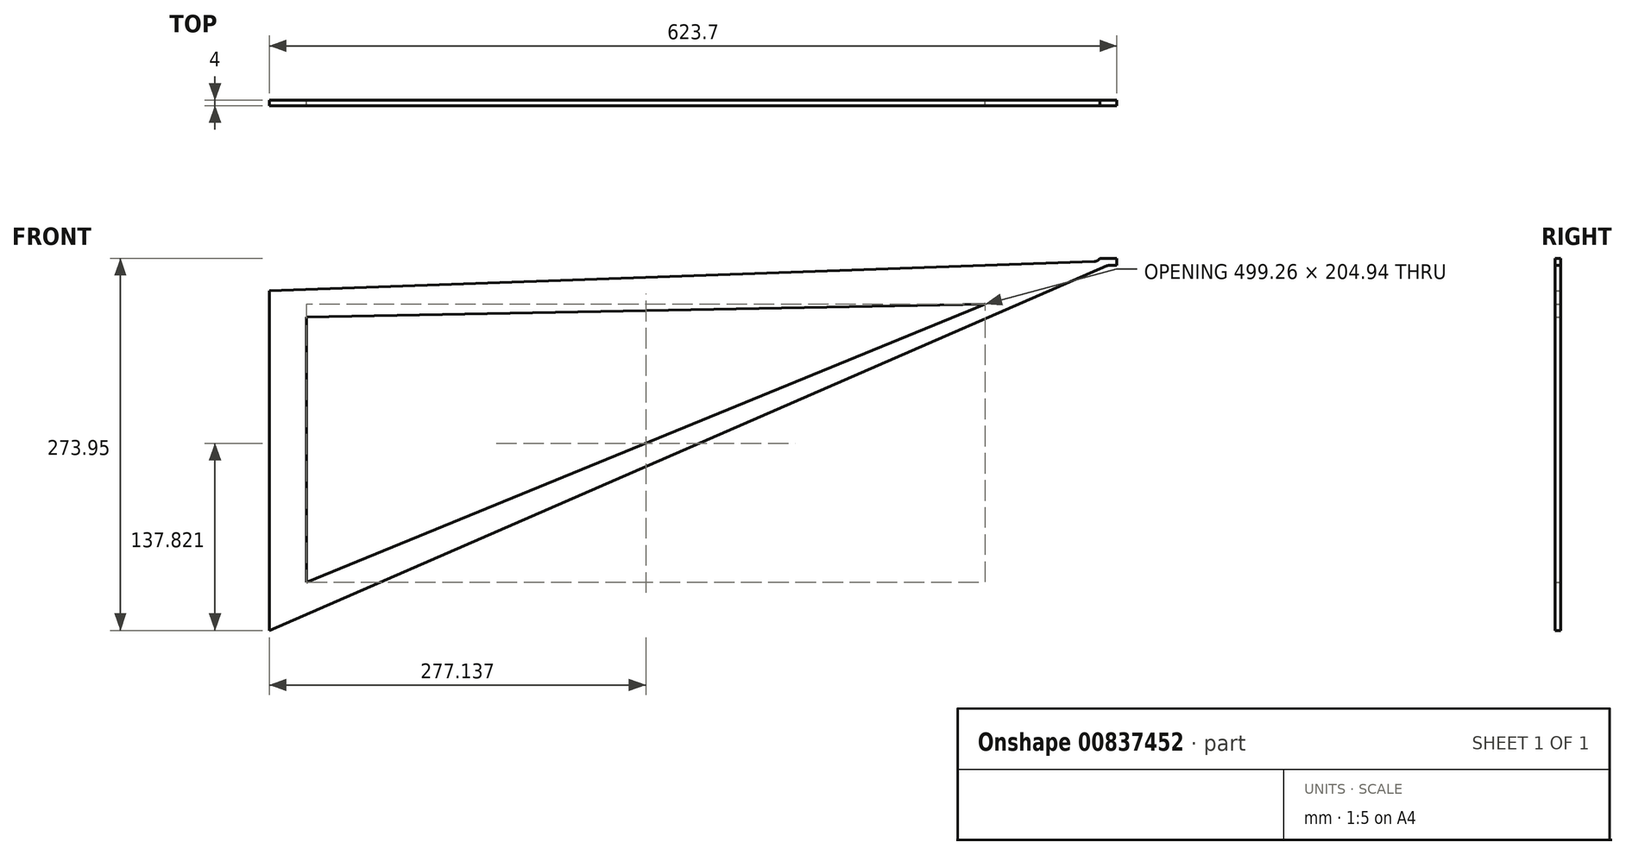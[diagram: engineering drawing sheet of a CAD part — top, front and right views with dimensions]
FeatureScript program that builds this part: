
annotation { "Feature Type Name" : "Feature", "Feature Type Description" : "" }
export const myFeature = defineFeature(function(context is Context, id is Id, definition is map)
    precondition{}
    {
        {
            var Q0;
            Q0=qCreatedBy(makeId("Front.planeOp"),FACE);
            var sketch = newSketch(context, id + "F0", { "sketchPlane" : qUnion([Q0])});
            skLineSegment(sketch, "E0", {"start": v(0, 0) * mm, "end": v(0, -250) * mm});
            skLineSegment(sketch, "E1", {"start": v(611.2, 21.85) * mm, "end": v(0, 0) * mm});
            skLineSegment(sketch, "E2.bottom", {"start": v(611.2, 18.95) * mm, "end": v(623.7, 18.95) * mm});
            skLineSegment(sketch, "E2.top", {"start": v(611.2, 23.95) * mm, "end": v(623.7, 23.95) * mm});
            skLineSegment(sketch, "E2.left", {"start": v(611.2, 18.95) * mm, "end": v(611.2, 23.95) * mm});
            skLineSegment(sketch, "E2.right", {"start": v(623.7, 18.95) * mm, "end": v(623.7, 23.95) * mm});
            skLineSegment(sketch, "E3", {"start": v(27.5, -19.3) * mm, "end": v(27.5, -214.65) * mm});
            skLineSegment(sketch, "E4", {"start": v(617.45, 18.95) * mm, "end": v(0, -250) * mm});
            skLineSegment(sketch, "E5", {"start": v(27.5, -214.65) * mm, "end": v(526.77, -9.71) * mm});
            skLineSegment(sketch, "E6", {"start": v(526.77, -9.71) * mm, "end": v(27.5, -19.3) * mm});
            skSolve(sketch);
        }
        {
            var Q0;
            Q0=makeQuery(id+"F0.imprint","IMPRINT",FACE,{"disambiguationData":[TD([[makeQuery(id+"F0.imprint","IMPRINT",EDGE,{"derivedFrom":sQuery(id+"F0.wireOp",EDGE,"E0")}),1.0]])]});
            extrude(context, id + "F1", {"entities" : qUnion([Q0]), "depth" : 2 * mm, "offsetDistance" : 25 * mm});
        }
        {
            var Q0;
            Q0=makeQuery(id+"F0.imprint","IMPRINT",FACE,{"disambiguationData":[TD([[makeQuery(id+"F0.imprint","IMPRINT",EDGE,{"derivedFrom":sQuery(id+"F0.wireOp",EDGE,"E0")}),1.0]])]});
            extrude(context, id + "F2", {"entities" : qUnion([Q0]), "operationType" : NewBodyOperationType.ADD, "oppositeDirection" : true, "depth" : 2 * mm, "offsetDistance" : 25 * mm});
        }
        {
            var Q0;
            {var subQ4=sQuery(id+"F0.wireOp",EDGE,"E2.top");Q0=makeQuery(id+"F0.imprint","IMPRINT",FACE,{"disambiguationData":[TD([[makeQuery(id+"F0.imprint","IMPRINT",EDGE,{"derivedFrom":subQ4}),-1.0]])]});}
            extrude(context, id + "F3", {"entities" : qUnion([Q0]), "operationType" : NewBodyOperationType.ADD, "depth" : 2 * mm, "offsetDistance" : 25 * mm});
        }
        {
            var Q0;
            {var subQ4=sQuery(id+"F0.wireOp",EDGE,"E2.top");Q0=makeQuery(id+"F0.imprint","IMPRINT",FACE,{"disambiguationData":[TD([[makeQuery(id+"F0.imprint","IMPRINT",EDGE,{"derivedFrom":subQ4}),-1.0]])]});}
            extrude(context, id + "F4", {"entities" : qUnion([Q0]), "operationType" : NewBodyOperationType.ADD, "oppositeDirection" : true, "depth" : 2 * mm, "offsetDistance" : 25 * mm});
        }
        {
            var Q0;
            {var subQ0=sQuery(id+"F0.wireOp",EDGE,"E1");var subQ3=sQuery(id+"F0.wireOp",EDGE,"E2.left");var subQ4=makeQuery(id+"F2.boolean.opBoolean","MERGE",EDGE,{"derivedFrom":[makeQuery(id+"F1.opExtrude","SWEPT_EDGE",EDGE,{"disambiguationData":[OSD([subQ0,subQ3])]}),makeQuery(id+"F2.opExtrude","SWEPT_EDGE",EDGE,{"disambiguationData":[OSD([subQ0,subQ3])]})]});Q0=makeQuery(id+"F4.boolean.opBoolean","MERGE",EDGE,{"derivedFrom":[makeQuery(id+"F3.boolean.opBoolean","SPLIT",EDGE,{"disambiguationData":[topologyDisambiguationEdgeConnected([makeQuery(id+"F1.opExtrude","SWEPT_FACE",FACE,{"disambiguationData":[OSD([subQ3])]})])],"derivedFrom":subQ4}),makeQuery(id+"F3.boolean.opBoolean","SPLIT",EDGE,{"disambiguationData":[topologyDisambiguationEdgeConnected([makeQuery(id+"F3.opExtrude","SWEPT_FACE",FACE,{"disambiguationData":[OSD([subQ3])]})])],"derivedFrom":subQ4})]});}
            fillet(context, id + "F5", {"entities" : qUnion([Q0]), "radius" : 5 * mm, "tangentPropagation" : true, "allowEdgeOverflow" : false});
        }
        {
            var Q0;
            {var subQ0=sQuery(id+"F0.wireOp",EDGE,"ZknlMTDO-dcBx-KLZg-5WCy-s5h5m6CvfQZP");var subQ3=sQuery(id+"F0.wireOp",EDGE,"E2.bottom");var subQ4=makeQuery(id+"F2.boolean.opBoolean","MERGE",EDGE,{"derivedFrom":[makeQuery(id+"F1.opExtrude","SWEPT_EDGE",EDGE,{"disambiguationData":[OSD([subQ0,subQ3])]}),makeQuery(id+"F2.opExtrude","SWEPT_EDGE",EDGE,{"disambiguationData":[OSD([subQ0,subQ3])]})]});Q0=makeQuery(id+"F4.boolean.opBoolean","MERGE",EDGE,{"derivedFrom":[makeQuery(id+"F3.boolean.opBoolean","SPLIT",EDGE,{"disambiguationData":[topologyDisambiguationEdgeConnected([makeQuery(id+"F1.opExtrude","SWEPT_FACE",FACE,{"disambiguationData":[OSD([subQ3])]})])],"derivedFrom":subQ4}),makeQuery(id+"F3.boolean.opBoolean","SPLIT",EDGE,{"disambiguationData":[topologyDisambiguationEdgeConnected([makeQuery(id+"F3.opExtrude","SWEPT_FACE",FACE,{"disambiguationData":[OSD([subQ3])]})])],"derivedFrom":subQ4})]});}
            fillet(context, id + "F6", {"entities" : qUnion([Q0]), "radius" : 6.5 * mm, "tangentPropagation" : true, "allowEdgeOverflow" : false});
        }
    });
